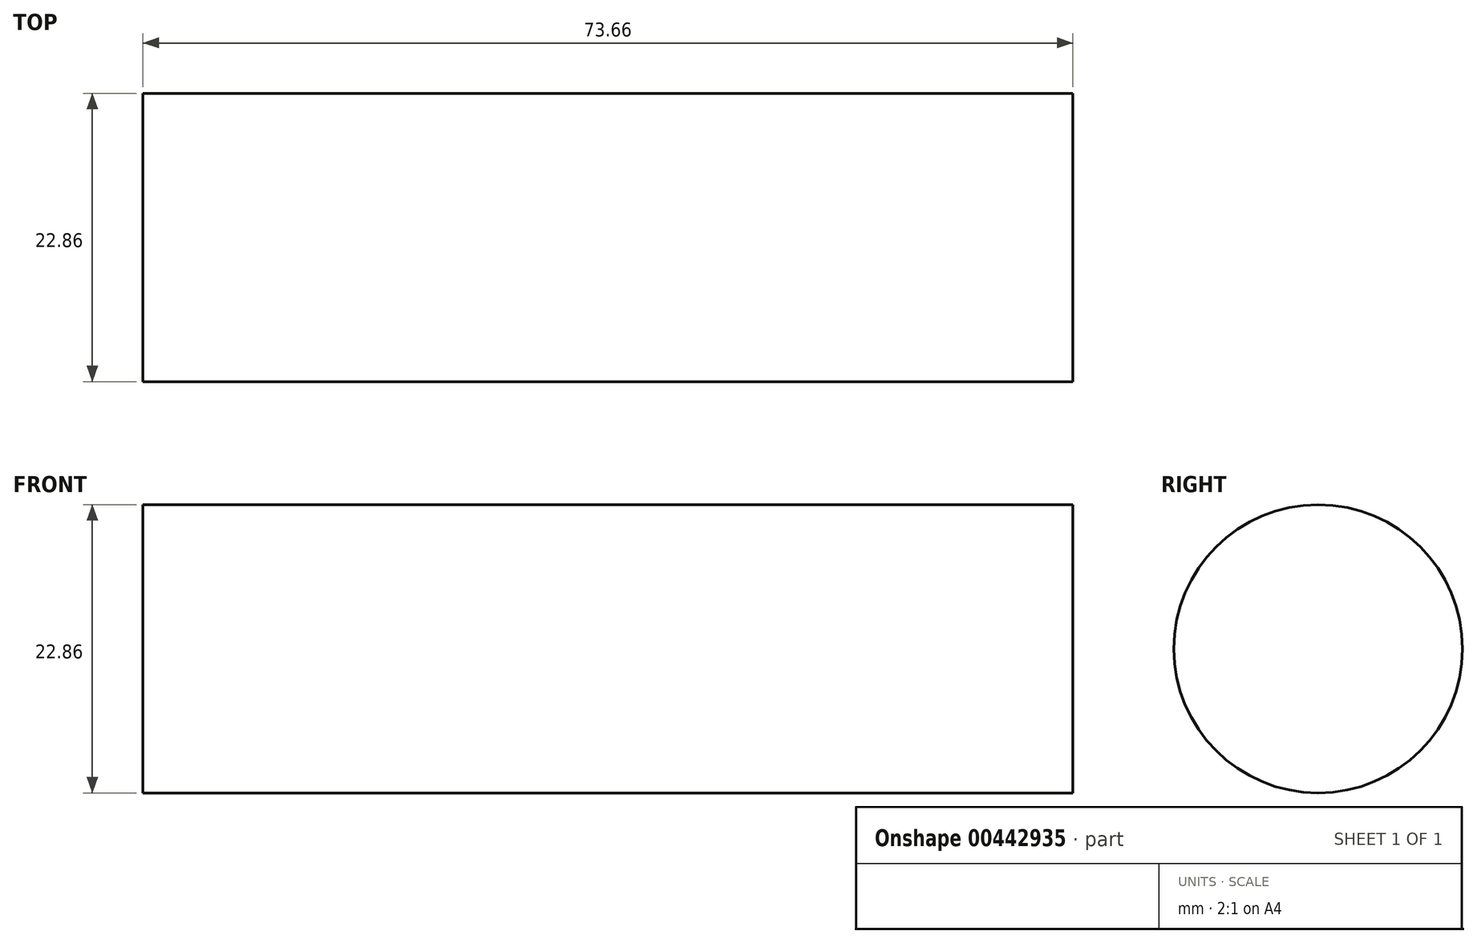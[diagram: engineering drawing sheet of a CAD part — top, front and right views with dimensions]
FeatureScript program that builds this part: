
annotation { "Feature Type Name" : "Feature", "Feature Type Description" : "" }
export const myFeature = defineFeature(function(context is Context, id is Id, definition is map)
    precondition{}
    {
        {
            var Q0;
            Q0=qCreatedBy(makeId("Right.planeOp"),FACE);
            var sketch = newSketch(context, id + "F0", { "sketchPlane" : qUnion([Q0])});
            skCircle(sketch, "E0", {"center": v(37.37, 44.64) * mm, "radius": 11.43 * mm});
            skSolve(sketch);
        }
        {
            var Q0;
            Q0=makeQuery(id+"F0.imprint","IMPRINT",FACE,{"disambiguationData":[TD([[makeQuery(id+"F0.imprint","IMPRINT",EDGE,{"derivedFrom":sQuery(id+"F0.wireOp",EDGE,"E0")}),1.0]])]});
            extrude(context, id + "F1", {"entities" : qUnion([Q0]), "depth" : 73.66 * mm});
        }
    });
